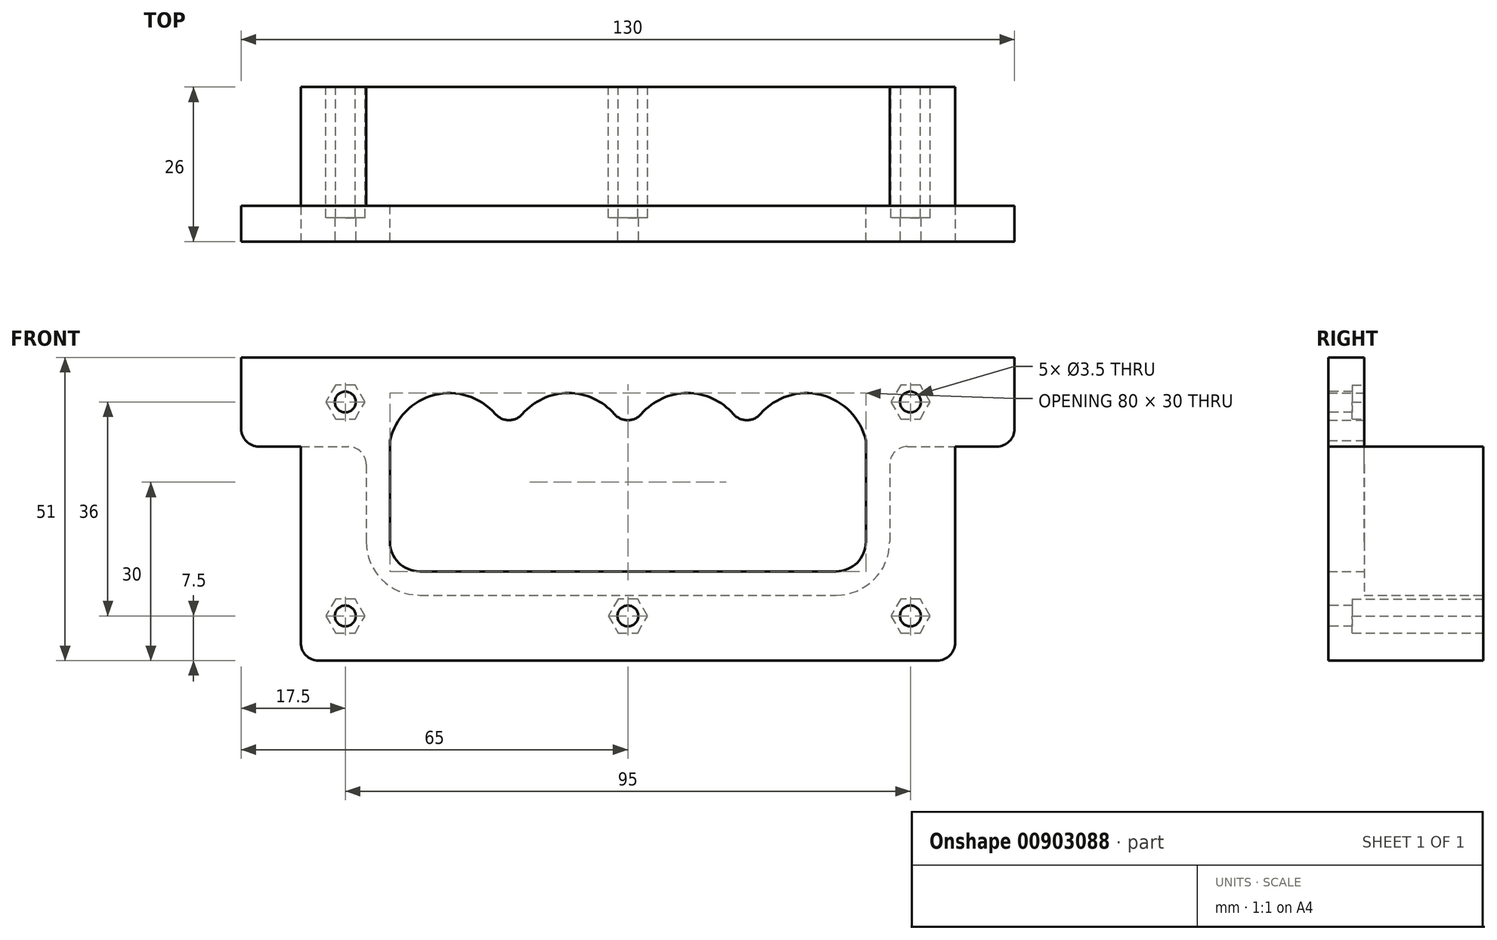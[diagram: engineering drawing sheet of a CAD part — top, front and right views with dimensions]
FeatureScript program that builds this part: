
annotation { "Feature Type Name" : "Feature", "Feature Type Description" : "" }
export const myFeature = defineFeature(function(context is Context, id is Id, definition is map)
    precondition{}
    {
        {
            var Q0;
            Q0=qCreatedBy(makeId("Front.planeOp"),FACE);
            var sketch = newSketch(context, id + "F0", { "sketchPlane" : qUnion([Q0])});
            skLineSegment(sketch, "E0.bottom", {"start": v(0, 0) * mm, "end": v(80, 0) * mm, "construction": true});
            skLineSegment(sketch, "E0.top", {"start": v(5, -30) * mm, "end": v(75, -30) * mm});
            skLineSegment(sketch, "E0.left", {"start": v(0, -8) * mm, "end": v(0, -25) * mm});
            skLineSegment(sketch, "E0.right", {"start": v(80, -8) * mm, "end": v(80, -25) * mm});
            skLineSegment(sketch, "E1", {"start": v(105, 6) * mm, "end": v(-25, 6) * mm});
            skLineSegment(sketch, "E2", {"start": v(-25, 6) * mm, "end": v(-25, -9) * mm});
            skLineSegment(sketch, "E3", {"start": v(-25, -9) * mm, "end": v(-15, -9) * mm});
            skLineSegment(sketch, "E4", {"start": v(-15, -9) * mm, "end": v(-15, -45) * mm});
            skLineSegment(sketch, "E5", {"start": v(-15, -45) * mm, "end": v(95, -45) * mm});
            skLineSegment(sketch, "E6", {"start": v(95, -45) * mm, "end": v(95, -9) * mm});
            skLineSegment(sketch, "E7", {"start": v(95, -9) * mm, "end": v(105, -9) * mm});
            skLineSegment(sketch, "E8", {"start": v(105, -9) * mm, "end": v(105, 6) * mm});
            skLineSegment(sketch, "E9", {"start": v(40, 0) * mm, "end": v(40, -8) * mm, "construction": true});
            skLineSegment(sketch, "E10", {"start": v(40, -8) * mm, "end": v(20, -8) * mm, "construction": true});
            skLineSegment(sketch, "E11", {"start": v(20, -8) * mm, "end": v(0, -8) * mm, "construction": true});
            skLineSegment(sketch, "E12", {"start": v(20, -8) * mm, "end": v(20, 0) * mm, "construction": true});
            skLineSegment(sketch, "E13", {"start": v(40, -8) * mm, "end": v(60, -8) * mm, "construction": true});
            skLineSegment(sketch, "E14", {"start": v(60, -8) * mm, "end": v(80, -8) * mm, "construction": true});
            skLineSegment(sketch, "E15", {"start": v(60, -8) * mm, "end": v(60, 0) * mm, "construction": true});
            skLineSegment(sketch, "E16", {"start": v(10, -8) * mm, "end": v(10, 0) * mm, "construction": true});
            skLineSegment(sketch, "E17", {"start": v(30, -8) * mm, "end": v(30, 0) * mm, "construction": true});
            skLineSegment(sketch, "E18", {"start": v(50, -8) * mm, "end": v(50, 0) * mm, "construction": true});
            skLineSegment(sketch, "E19", {"start": v(70, -8) * mm, "end": v(70, 0) * mm, "construction": true});
            skArc(sketch, "E20", {"start": v(17.74, -3.53) * mm, "mid": v(7.5, -0.31) * mm, "end": v(0, -8) * mm});
            skArc(sketch, "E21", {"start": v(37.74, -3.53) * mm, "mid": v(30, 0) * mm, "end": v(22.26, -3.53) * mm});
            skArc(sketch, "E22", {"start": v(57.74, -3.53) * mm, "mid": v(50, 0) * mm, "end": v(42.26, -3.53) * mm});
            skArc(sketch, "E23", {"start": v(80, -8) * mm, "mid": v(72.5, -0.31) * mm, "end": v(62.26, -3.53) * mm});
            skLineSegment(sketch, "E24", {"start": v(0, -8) * mm, "end": v(0, 0) * mm, "construction": true});
            skLineSegment(sketch, "E25", {"start": v(80, -8) * mm, "end": v(80, 0) * mm, "construction": true});
            skPoint(sketch, "E26.visualSharp", {"position": v(0, -30) * mm});
            skArc(sketch, "E26.filletArc", {"start": v(0, -25) * mm, "mid": v(1.46, -28.54) * mm, "end": v(5, -30) * mm});
            skPoint(sketch, "E27.visualSharp", {"position": v(80, -30) * mm});
            skArc(sketch, "E27.filletArc", {"start": v(75, -30) * mm, "mid": v(78.54, -28.54) * mm, "end": v(80, -25) * mm});
            skPoint(sketch, "E28.visualSharp", {"position": v(20, -8) * mm});
            skArc(sketch, "E28.filletArc", {"start": v(17.74, -3.53) * mm, "mid": v(20, -4.56) * mm, "end": v(22.26, -3.53) * mm});
            skPoint(sketch, "E29.visualSharp", {"position": v(40, -8) * mm});
            skArc(sketch, "E29.filletArc", {"start": v(37.74, -3.53) * mm, "mid": v(40, -4.56) * mm, "end": v(42.26, -3.53) * mm});
            skPoint(sketch, "E30.visualSharp", {"position": v(60, -8) * mm});
            skArc(sketch, "E30.filletArc", {"start": v(57.74, -3.53) * mm, "mid": v(60, -4.56) * mm, "end": v(62.26, -3.53) * mm});
            skSolve(sketch);
        }
        {
            var Q0;
            Q0=makeQuery(id+"F0.imprint","IMPRINT",FACE,{"disambiguationData":[TD([[makeQuery(id+"F0.imprint","IMPRINT",EDGE,{"derivedFrom":sQuery(id+"F0.wireOp",EDGE,"E0.top")}),-1.0]])]});
            var Q1;
            Q1=makeQuery(id+"F0.imprint","IMPRINT",FACE,{"disambiguationData":[TD([[makeQuery(id+"F0.imprint","IMPRINT",EDGE,{"derivedFrom":sQuery(id+"F0.wireOp",EDGE,"E0.top")}),1.0]])]});
            extrude(context, id + "F1", {"entities" : qUnion([Q0, Q1]), "oppositeDirection" : true, "depth" : 6 * mm, "offsetDistance" : 25 * mm});
        }
        {
            var Q0;
            Q0 = qSketchRegion(id + "F0", true);
            extrude(context, id + "F2", {"entities" : qUnion([Q0]), "operationType" : NewBodyOperationType.ADD, "depth" : 20 * mm, "offsetDistance" : 25 * mm});
        }
        {
            var Q0;
            {var subQ0=sQuery(id+"F0.wireOp",EDGE,"E7");Q0=makeQuery(id+"F2.boolean.opBoolean","MERGE",FACE,{"derivedFrom":[makeQuery(id+"F1.opExtrude","SWEPT_FACE",FACE,{"disambiguationData":[OSD([subQ0])]}),makeQuery(id+"F2.opExtrude","SWEPT_FACE",FACE,{"disambiguationData":[OSD([subQ0])]})]});}
            var sketch = newSketch(context, id + "F3", { "sketchPlane" : qUnion([Q0])});
            skCircle(sketch, "E31", {"center": v(97.5, 10) * mm, "radius": 2.75 * mm});
            skCircle(sketch, "E32", {"center": v(-17.5, 10) * mm, "radius": 2.75 * mm});
            skSolve(sketch);
        }
        {
            var Q0;
            Q0 = qSketchRegion(id + "F3", true);
            var Q1;
            {var subQ0=sQuery(id+"F0.wireOp",EDGE,"E1");Q1=makeQuery(id+"F2.boolean.opBoolean","MERGE",FACE,{"derivedFrom":[makeQuery(id+"F1.opExtrude","SWEPT_FACE",FACE,{"disambiguationData":[OSD([subQ0])]}),makeQuery(id+"F2.opExtrude","SWEPT_FACE",FACE,{"disambiguationData":[OSD([subQ0])]})]});}
            extrude(context, id + "F4", {"entities" : qUnion([Q0]), "operationType" : NewBodyOperationType.REMOVE, "endBound" : BoundingType.UP_TO_SURFACE, "oppositeDirection" : true, "depth" : 25 * mm, "endBoundEntityFace" : qUnion([Q1]), "offsetDistance" : 25 * mm});
        }
        {
            var Q0;
            Q0=makeQuery(id+"F2.opExtrude","CAP_FACE",FACE,{"disambiguationData":[OSD([sQuery(id+"F0.wireOp",EDGE,"E0.bottom"),sQuery(id+"F0.wireOp",EDGE,"E0.top"),sQuery(id+"F0.wireOp",EDGE,"E0.left"),sQuery(id+"F0.wireOp",EDGE,"E0.right"),sQuery(id+"F0.wireOp",EDGE,"E1"),sQuery(id+"F0.wireOp",EDGE,"E2"),sQuery(id+"F0.wireOp",EDGE,"E3"),sQuery(id+"F0.wireOp",EDGE,"E4"),sQuery(id+"F0.wireOp",EDGE,"E5"),sQuery(id+"F0.wireOp",EDGE,"E6"),sQuery(id+"F0.wireOp",EDGE,"E7"),sQuery(id+"F0.wireOp",EDGE,"E8")])],"isStart":false});
            var sketch = newSketch(context, id + "F5", { "sketchPlane" : qUnion([Q0])});
            skLineSegment(sketch, "E33", {"start": v(87.5, -1.5) * mm, "end": v(87.5, -37.5) * mm, "construction": true});
            skLineSegment(sketch, "E34", {"start": v(87.5, -37.5) * mm, "end": v(-7.5, -37.5) * mm, "construction": true});
            skLineSegment(sketch, "E35", {"start": v(-7.5, -37.5) * mm, "end": v(-7.5, -1.5) * mm, "construction": true});
            skCircle(sketch, "E36", {"center": v(40, -37.5) * mm, "radius": 1.75 * mm});
            skCircle(sketch, "E37", {"center": v(-7.5, -37.5) * mm, "radius": 1.75 * mm});
            skCircle(sketch, "E38", {"center": v(-7.5, -1.5) * mm, "radius": 1.75 * mm});
            skCircle(sketch, "E39", {"center": v(87.5, -1.5) * mm, "radius": 1.75 * mm});
            skCircle(sketch, "E40", {"center": v(87.5, -37.5) * mm, "radius": 1.75 * mm});
            skSolve(sketch);
        }
        {
            var Q0;
            Q0 = qSketchRegion(id + "F5", true);
            var Q1;
            Q1=makeQuery(id+"F1.opExtrude","CAP_FACE",FACE,{"disambiguationData":[OSD([sQuery(id+"F0.wireOp",EDGE,"E1"),sQuery(id+"F0.wireOp",EDGE,"E2"),sQuery(id+"F0.wireOp",EDGE,"E3"),sQuery(id+"F0.wireOp",EDGE,"E4"),sQuery(id+"F0.wireOp",EDGE,"E5"),sQuery(id+"F0.wireOp",EDGE,"E6"),sQuery(id+"F0.wireOp",EDGE,"E7"),sQuery(id+"F0.wireOp",EDGE,"E8")])],"isStart":false});
            extrude(context, id + "F6", {"entities" : qUnion([Q0]), "operationType" : NewBodyOperationType.REMOVE, "endBound" : BoundingType.UP_TO_SURFACE, "oppositeDirection" : true, "depth" : 25 * mm, "endBoundEntityFace" : qUnion([Q1]), "offsetDistance" : 25 * mm});
        }
        {
            var Q0;
            Q0=makeQuery(id+"F1.opExtrude","CAP_FACE",FACE,{"disambiguationData":[OSD([sQuery(id+"F0.wireOp",EDGE,"E1"),sQuery(id+"F0.wireOp",EDGE,"E2"),sQuery(id+"F0.wireOp",EDGE,"E3"),sQuery(id+"F0.wireOp",EDGE,"E4"),sQuery(id+"F0.wireOp",EDGE,"E5"),sQuery(id+"F0.wireOp",EDGE,"E6"),sQuery(id+"F0.wireOp",EDGE,"E7"),sQuery(id+"F0.wireOp",EDGE,"E8")])],"isStart":false});
            var sketch = newSketch(context, id + "F7", { "sketchPlane" : qUnion([Q0])});
            skCircle(sketch, "E41.cCircle", {"center": v(7.5, -1.5) * mm, "radius": 2.85 * mm, "construction": true});
            skLineSegment(sketch, "E41.0", {"start": v(9.15, 1.35) * mm, "end": v(10.8, -1.5) * mm});
            skLineSegment(sketch, "E41.1", {"start": v(10.8, -1.5) * mm, "end": v(9.15, -4.35) * mm});
            skLineSegment(sketch, "E41.2", {"start": v(9.15, -4.35) * mm, "end": v(5.85, -4.35) * mm});
            skLineSegment(sketch, "E41.3", {"start": v(5.85, -4.35) * mm, "end": v(4.2, -1.5) * mm});
            skLineSegment(sketch, "E41.4", {"start": v(4.2, -1.5) * mm, "end": v(5.85, 1.35) * mm});
            skLineSegment(sketch, "E41.5", {"start": v(5.85, 1.35) * mm, "end": v(9.15, 1.35) * mm});
            skPoint(sketch, "E41.0.midPoint", {"position": v(9.97, -0.08) * mm});
            skCircle(sketch, "E42.cCircle", {"center": v(7.5, -37.5) * mm, "radius": 2.85 * mm, "construction": true});
            skLineSegment(sketch, "E42.0", {"start": v(4.2, -37.5) * mm, "end": v(5.85, -34.65) * mm});
            skLineSegment(sketch, "E42.1", {"start": v(5.85, -34.65) * mm, "end": v(9.15, -34.65) * mm});
            skLineSegment(sketch, "E42.2", {"start": v(9.15, -34.65) * mm, "end": v(10.8, -37.5) * mm});
            skLineSegment(sketch, "E42.3", {"start": v(10.8, -37.5) * mm, "end": v(9.15, -40.35) * mm});
            skLineSegment(sketch, "E42.4", {"start": v(9.15, -40.35) * mm, "end": v(5.85, -40.35) * mm});
            skLineSegment(sketch, "E42.5", {"start": v(5.85, -40.35) * mm, "end": v(4.2, -37.5) * mm});
            skPoint(sketch, "E42.0.midPoint", {"position": v(5.03, -36.07) * mm});
            skCircle(sketch, "E43.cCircle", {"center": v(-40, -37.5) * mm, "radius": 2.85 * mm, "construction": true});
            skLineSegment(sketch, "E43.0", {"start": v(-38.35, -34.65) * mm, "end": v(-36.7, -37.5) * mm});
            skLineSegment(sketch, "E43.1", {"start": v(-36.7, -37.5) * mm, "end": v(-38.35, -40.35) * mm});
            skLineSegment(sketch, "E43.2", {"start": v(-38.35, -40.35) * mm, "end": v(-41.65, -40.35) * mm});
            skLineSegment(sketch, "E43.3", {"start": v(-41.65, -40.35) * mm, "end": v(-43.3, -37.5) * mm});
            skLineSegment(sketch, "E43.4", {"start": v(-43.3, -37.5) * mm, "end": v(-41.65, -34.65) * mm});
            skLineSegment(sketch, "E43.5", {"start": v(-41.65, -34.65) * mm, "end": v(-38.35, -34.65) * mm});
            skPoint(sketch, "E43.0.midPoint", {"position": v(-37.53, -36.07) * mm});
            skCircle(sketch, "E44.cCircle", {"center": v(-87.5, -37.5) * mm, "radius": 2.85 * mm, "construction": true});
            skLineSegment(sketch, "E44.0", {"start": v(-85.85, -34.65) * mm, "end": v(-84.2, -37.5) * mm});
            skLineSegment(sketch, "E44.1", {"start": v(-84.2, -37.5) * mm, "end": v(-85.85, -40.35) * mm});
            skLineSegment(sketch, "E44.2", {"start": v(-85.85, -40.35) * mm, "end": v(-89.15, -40.35) * mm});
            skLineSegment(sketch, "E44.3", {"start": v(-89.15, -40.35) * mm, "end": v(-90.8, -37.5) * mm});
            skLineSegment(sketch, "E44.4", {"start": v(-90.8, -37.5) * mm, "end": v(-89.15, -34.65) * mm});
            skLineSegment(sketch, "E44.5", {"start": v(-89.15, -34.65) * mm, "end": v(-85.85, -34.65) * mm});
            skPoint(sketch, "E44.0.midPoint", {"position": v(-85.03, -36.07) * mm});
            skCircle(sketch, "E45.cCircle", {"center": v(-87.5, -1.5) * mm, "radius": 2.85 * mm, "construction": true});
            skLineSegment(sketch, "E45.0", {"start": v(-85.85, 1.35) * mm, "end": v(-84.2, -1.5) * mm});
            skLineSegment(sketch, "E45.1", {"start": v(-84.2, -1.5) * mm, "end": v(-85.85, -4.35) * mm});
            skLineSegment(sketch, "E45.2", {"start": v(-85.85, -4.35) * mm, "end": v(-89.15, -4.35) * mm});
            skLineSegment(sketch, "E45.3", {"start": v(-89.15, -4.35) * mm, "end": v(-90.8, -1.5) * mm});
            skLineSegment(sketch, "E45.4", {"start": v(-90.8, -1.5) * mm, "end": v(-89.15, 1.35) * mm});
            skLineSegment(sketch, "E45.5", {"start": v(-89.15, 1.35) * mm, "end": v(-85.85, 1.35) * mm});
            skPoint(sketch, "E45.0.midPoint", {"position": v(-85.03, -0.08) * mm});
            skSolve(sketch);
        }
        {
            var Q0;
            Q0 = qSketchRegion(id + "F7", true);
            extrude(context, id + "F8", {"entities" : qUnion([Q0]), "operationType" : NewBodyOperationType.REMOVE, "oppositeDirection" : true, "depth" : 22 * mm, "offsetDistance" : 25 * mm});
        }
        {
            var Q0;
            Q0=makeQuery(id+"F1.opExtrude","CAP_FACE",FACE,{"disambiguationData":[OSD([sQuery(id+"F0.wireOp",EDGE,"E1"),sQuery(id+"F0.wireOp",EDGE,"E2"),sQuery(id+"F0.wireOp",EDGE,"E3"),sQuery(id+"F0.wireOp",EDGE,"E4"),sQuery(id+"F0.wireOp",EDGE,"E5"),sQuery(id+"F0.wireOp",EDGE,"E6"),sQuery(id+"F0.wireOp",EDGE,"E7"),sQuery(id+"F0.wireOp",EDGE,"E8")])],"isStart":false});
            var sketch = newSketch(context, id + "F9", { "sketchPlane" : qUnion([Q0])});
            skArc(sketch, "E46.0", {"start": v(4, -25) * mm, "mid": v(1.36, -31.36) * mm, "end": v(-5, -34) * mm});
            skLineSegment(sketch, "E46.1", {"start": v(4, -9) * mm, "end": v(4, -25) * mm});
            skLineSegment(sketch, "E46.2", {"start": v(-5, -34) * mm, "end": v(-75, -34) * mm});
            skArc(sketch, "E46.5", {"start": v(-75, -34) * mm, "mid": v(-81.36, -31.36) * mm, "end": v(-84, -25) * mm});
            skLineSegment(sketch, "E46.6", {"start": v(-84, -9) * mm, "end": v(-84, -25) * mm});
            skLineSegment(sketch, "E47", {"start": v(15, -9) * mm, "end": v(4, -9) * mm});
            skLineSegment(sketch, "E48", {"start": v(-95, -9) * mm, "end": v(-84, -9) * mm});
            skLineSegment(sketch, "E49", {"start": v(-95, -9) * mm, "end": v(-95, -45) * mm});
            skLineSegment(sketch, "E50", {"start": v(-95, -45) * mm, "end": v(15, -45) * mm});
            skLineSegment(sketch, "E51", {"start": v(15, -45) * mm, "end": v(15, -9) * mm});
            skCircle(sketch, "E52", {"center": v(-87.5, -1.5) * mm, "radius": 4.5 * mm});
            skCircle(sketch, "E53", {"center": v(7.5, -1.5) * mm, "radius": 4.5 * mm});
            skSolve(sketch);
        }
        {
            var Q0;
            {var subQ5=makeQuery(id+"F8.boolean.opBoolean","COPY",EDGE,{"derivedFrom":makeQuery(id+"F8.opExtrude","CAP_EDGE",EDGE,{"disambiguationData":[OSD([sQuery(id+"F7.wireOp",EDGE,"E43.5")])],"isStart":true})});Q0=makeQuery(id+"F9.imprint","IMPRINT",FACE,{"disambiguationData":[TD([[makeQuery(id+"F9.imprint","IMPRINT",EDGE,{"derivedFrom":subQ5}),-1.0]])]});}
            var Q1;
            {var subQ3=sQuery(id+"F9.wireOp",EDGE,"E46.0");Q1=makeQuery(id+"F9.imprint","IMPRINT",FACE,{"disambiguationData":[TD([[makeQuery(id+"F9.imprint","IMPRINT",EDGE,{"derivedFrom":subQ3}),1.0]])]});}
            var Q2;
            Q2=makeQuery(id+"F9.imprint","IMPRINT",FACE,{"disambiguationData":[TD([[makeQuery(id+"F9.imprint","IMPRINT",EDGE,{"derivedFrom":sQuery(id+"F9.wireOp",EDGE,"E53")}),1.0]])]});
            var Q3;
            Q3=makeQuery(id+"F9.imprint","IMPRINT",FACE,{"disambiguationData":[TD([[makeQuery(id+"F9.imprint","IMPRINT",EDGE,{"derivedFrom":sQuery(id+"F9.wireOp",EDGE,"E52")}),1.0]])]});
            extrude(context, id + "F10", {"entities" : qUnion([Q0, Q1, Q2, Q3]), "operationType" : NewBodyOperationType.REMOVE, "oppositeDirection" : true, "depth" : 20 * mm, "offsetDistance" : 25 * mm});
        }
        {
            var Q0;
            {var subQ0=sQuery(id+"F0.wireOp",EDGE,"E3");Q0=makeQuery(id+"F10.boolean.opBoolean","MERGE",FACE,{"derivedFrom":[makeQuery(id+"F2.boolean.opBoolean","MERGE",FACE,{"derivedFrom":[makeQuery(id+"F1.opExtrude","SWEPT_FACE",FACE,{"disambiguationData":[OSD([subQ0])]}),makeQuery(id+"F2.opExtrude","SWEPT_FACE",FACE,{"disambiguationData":[OSD([subQ0])]})]})],"fromTools":[makeQuery(id+"F10.opExtrude","SWEPT_FACE",FACE,{"disambiguationData":[OSD([sQuery(id+"F9.wireOp",EDGE,"E47")])]})]});}
            var sketch = newSketch(context, id + "F11", { "sketchPlane" : qUnion([Q0])});
            skCircle(sketch, "E54", {"center": v(-17.5, 10) * mm, "radius": 4.5 * mm});
            skCircle(sketch, "E55", {"center": v(97.5, 10) * mm, "radius": 4.5 * mm});
            skSolve(sketch);
        }
        {
            var Q0;
            Q0 = qSketchRegion(id + "F11", true);
            extrude(context, id + "F12", {"entities" : qUnion([Q0]), "operationType" : NewBodyOperationType.REMOVE, "oppositeDirection" : true, "depth" : 6 * mm, "offsetDistance" : 25 * mm});
        }
        {
            var Q0;
            Q0=makeQuery(id+"F10.boolean.opBoolean","COPY",EDGE,{"derivedFrom":makeQuery(id+"F10.opExtrude","CAP_EDGE",EDGE,{"disambiguationData":[OSD([sQuery(id+"F9.wireOp",EDGE,"E50")])],"isStart":false})});
            var Q1;
            Q1=makeQuery(id+"F10.boolean.opBoolean","COPY",EDGE,{"derivedFrom":makeQuery(id+"F10.opExtrude","CAP_EDGE",EDGE,{"disambiguationData":[OSD([sQuery(id+"F9.wireOp",EDGE,"E49")])],"isStart":false})});
            var Q2;
            Q2=makeQuery(id+"F10.boolean.opBoolean","COPY",EDGE,{"derivedFrom":makeQuery(id+"F10.opExtrude","CAP_EDGE",EDGE,{"disambiguationData":[OSD([sQuery(id+"F9.wireOp",EDGE,"E51")])],"isStart":false})});
            var Q3;
            Q3=makeQuery(id+"F10.boolean.opBoolean","COPY",EDGE,{"derivedFrom":makeQuery(id+"F10.opExtrude","CAP_EDGE",EDGE,{"disambiguationData":[OSD([sQuery(id+"F9.wireOp",EDGE,"E46.2")])],"isStart":true})});
            var Q4;
            Q4=makeQuery(id+"F10.boolean.opBoolean","MERGE",EDGE,{"derivedFrom":[makeQuery(id+"F1.opExtrude","CAP_EDGE",EDGE,{"disambiguationData":[OSD([sQuery(id+"F0.wireOp",EDGE,"E7")])],"isStart":false})],"fromTools":[makeQuery(id+"F10.opExtrude","CAP_EDGE",EDGE,{"disambiguationData":[OSD([sQuery(id+"F9.wireOp",EDGE,"E48")])],"isStart":true})]});
            var Q5;
            Q5=makeQuery(id+"F10.boolean.opBoolean","MERGE",EDGE,{"derivedFrom":[makeQuery(id+"F1.opExtrude","CAP_EDGE",EDGE,{"disambiguationData":[OSD([sQuery(id+"F0.wireOp",EDGE,"E3")])],"isStart":false})],"fromTools":[makeQuery(id+"F10.opExtrude","CAP_EDGE",EDGE,{"disambiguationData":[OSD([sQuery(id+"F9.wireOp",EDGE,"E47")])],"isStart":true})]});
            var Q6;
            Q6=makeQuery(id+"F1.opExtrude","CAP_EDGE",EDGE,{"disambiguationData":[OSD([sQuery(id+"F0.wireOp",EDGE,"E2")])],"isStart":false});
            var Q7;
            Q7=makeQuery(id+"F1.opExtrude","CAP_EDGE",EDGE,{"disambiguationData":[OSD([sQuery(id+"F0.wireOp",EDGE,"E8")])],"isStart":false});
            var Q8;
            {var subQ0=sQuery(id+"F0.wireOp",EDGE,"E8");var subQ1=sQuery(id+"F0.wireOp",EDGE,"E7");Q8=makeQuery(id+"F2.boolean.opBoolean","MERGE",EDGE,{"derivedFrom":[makeQuery(id+"F1.opExtrude","SWEPT_EDGE",EDGE,{"disambiguationData":[OSD([subQ1,subQ0])]}),makeQuery(id+"F2.opExtrude","SWEPT_EDGE",EDGE,{"disambiguationData":[OSD([subQ1,subQ0])]})]});}
            var Q9;
            Q9=makeQuery(id+"F10.boolean.opBoolean","COPY",EDGE,{"derivedFrom":makeQuery(id+"F10.opExtrude","SWEPT_EDGE",EDGE,{"disambiguationData":[OSD([sQuery(id+"F9.wireOp",EDGE,"E46.6"),sQuery(id+"F9.wireOp",EDGE,"E48")])]})});
            var Q10;
            Q10=makeQuery(id+"F10.boolean.opBoolean","COPY",EDGE,{"derivedFrom":makeQuery(id+"F10.opExtrude","SWEPT_EDGE",EDGE,{"disambiguationData":[OSD([sQuery(id+"F9.wireOp",EDGE,"E46.1"),sQuery(id+"F9.wireOp",EDGE,"E47")])]})});
            var Q11;
            {var subQ0=sQuery(id+"F0.wireOp",EDGE,"E5");var subQ1=sQuery(id+"F0.wireOp",EDGE,"E4");Q11=makeQuery(id+"F2.boolean.opBoolean","MERGE",EDGE,{"derivedFrom":[makeQuery(id+"F1.opExtrude","SWEPT_EDGE",EDGE,{"disambiguationData":[OSD([subQ1,subQ0])]}),makeQuery(id+"F2.opExtrude","SWEPT_EDGE",EDGE,{"disambiguationData":[OSD([subQ1,subQ0])]})]});}
            var Q12;
            {var subQ0=sQuery(id+"F0.wireOp",EDGE,"E6");var subQ1=sQuery(id+"F0.wireOp",EDGE,"E5");Q12=makeQuery(id+"F2.boolean.opBoolean","MERGE",EDGE,{"derivedFrom":[makeQuery(id+"F1.opExtrude","SWEPT_EDGE",EDGE,{"disambiguationData":[OSD([subQ1,subQ0])]}),makeQuery(id+"F2.opExtrude","SWEPT_EDGE",EDGE,{"disambiguationData":[OSD([subQ1,subQ0])]})]});}
            var Q13;
            {var subQ0=sQuery(id+"F0.wireOp",EDGE,"E3");var subQ1=sQuery(id+"F0.wireOp",EDGE,"E2");Q13=makeQuery(id+"F2.boolean.opBoolean","MERGE",EDGE,{"derivedFrom":[makeQuery(id+"F1.opExtrude","SWEPT_EDGE",EDGE,{"disambiguationData":[OSD([subQ1,subQ0])]}),makeQuery(id+"F2.opExtrude","SWEPT_EDGE",EDGE,{"disambiguationData":[OSD([subQ1,subQ0])]})]});}
            var Q14;
            Q14=makeQuery(id+"F1.opExtrude","CAP_EDGE",EDGE,{"disambiguationData":[OSD([sQuery(id+"F0.wireOp",EDGE,"E1")])],"isStart":false});
            var Q15;
            Q15=makeQuery(id+"F2.opExtrude","CAP_EDGE",EDGE,{"disambiguationData":[OSD([sQuery(id+"F0.wireOp",EDGE,"E0.left")])],"isStart":true});
            var Q16;
            Q16=makeQuery(id+"F2.opExtrude","CAP_EDGE",EDGE,{"disambiguationData":[OSD([sQuery(id+"F0.wireOp",EDGE,"E21")])],"isStart":true});
            var Q17;
            Q17=makeQuery(id+"F10.boolean.opBoolean","COPY",EDGE,{"derivedFrom":makeQuery(id+"F10.opExtrude","CAP_EDGE",EDGE,{"disambiguationData":[OSD([sQuery(id+"F9.wireOp",EDGE,"E52")])],"isStart":true})});
            var Q18;
            Q18=makeQuery(id+"F10.boolean.opBoolean","COPY",EDGE,{"derivedFrom":makeQuery(id+"F10.opExtrude","CAP_EDGE",EDGE,{"disambiguationData":[OSD([sQuery(id+"F9.wireOp",EDGE,"E53")])],"isStart":true})});
            fillet(context, id + "F13", {"entities" : qUnion([Q0, Q1, Q2, Q3, Q4, Q5, Q6, Q7, Q8, Q9, Q10, Q11, Q12, Q13, Q14, Q15, Q16, Q17, Q18]), "radius" : 3 * mm, "tangentPropagation" : true, "allowEdgeOverflow" : false});
        }
    });
